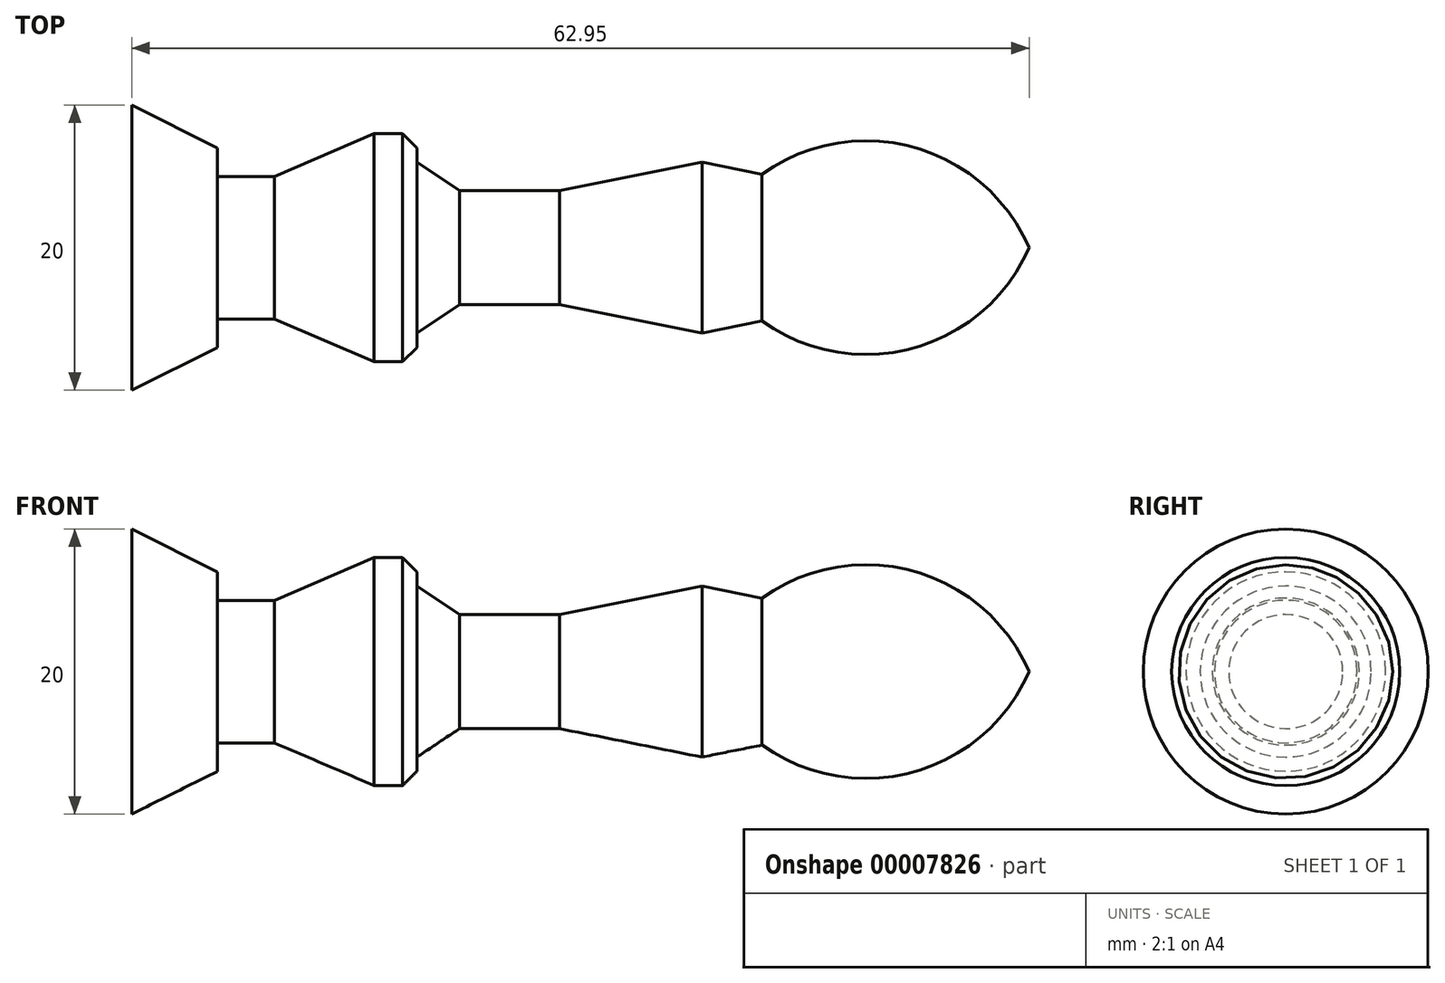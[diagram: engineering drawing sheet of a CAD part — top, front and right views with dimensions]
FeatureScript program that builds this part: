
annotation { "Feature Type Name" : "Feature", "Feature Type Description" : "" }
export const myFeature = defineFeature(function(context is Context, id is Id, definition is map)
    precondition{}
    {
        {
            var Q0;
            Q0=qCreatedBy(makeId("Front.planeOp"),FACE);
            var sketch = newSketch(context, id + "F0", { "sketchPlane" : qUnion([Q0])});
            skLineSegment(sketch, "E0", {"start": v(37.27, 0) * mm, "end": v(-27.73, 0) * mm});
            skLineSegment(sketch, "E1", {"start": v(16.48, -5.16) * mm, "end": v(12.27, -6) * mm});
            skLineSegment(sketch, "E2", {"start": v(12.27, -6) * mm, "end": v(2.27, -4) * mm});
            skLineSegment(sketch, "E3", {"start": v(2.27, -4) * mm, "end": v(-4.73, -4) * mm});
            skLineSegment(sketch, "E4", {"start": v(-4.73, -4) * mm, "end": v(-7.73, -6) * mm});
            skLineSegment(sketch, "E5", {"start": v(-7.73, -6) * mm, "end": v(-7.73, -8) * mm});
            skLineSegment(sketch, "E6", {"start": v(-7.73, -8) * mm, "end": v(-10.73, -8) * mm});
            skLineSegment(sketch, "E7", {"start": v(-10.73, -8) * mm, "end": v(-17.73, -5) * mm});
            skLineSegment(sketch, "E8", {"start": v(-17.73, -5) * mm, "end": v(-21.73, -5) * mm});
            skLineSegment(sketch, "E9", {"start": v(-21.73, -5) * mm, "end": v(-21.73, -7) * mm});
            skLineSegment(sketch, "E10", {"start": v(-21.73, -7) * mm, "end": v(-27.73, -10) * mm});
            skLineSegment(sketch, "E11", {"start": v(-27.73, -10) * mm, "end": v(-27.73, 0) * mm});
            skArc(sketch, "E12.trimOffspring", {"start": v(16.48, -5.16) * mm, "mid": v(27.08, -7.05) * mm, "end": v(35.22, 0) * mm});
            skSolve(sketch);
        }
        {
            var Q0;
            Q0=makeQuery(id+"F0.imprint","IMPRINT",FACE,{"disambiguationData":[TD([[makeQuery(id+"F0.imprint","IMPRINT",EDGE,{"derivedFrom":sQuery(id+"F0.wireOp",EDGE,"E1")}),-1.0]])]});
            var Q1;
            Q1=sQuery(id+"F0.wireOp",EDGE,"E0");
            revolve(context, id + "F1", {"entities" : qUnion([Q0]), "axis" : qUnion([Q1]), "revolveType" : RevolveType.FULL});
        }
        {
            var Q0;
            Q0=makeQuery(id+"F1.opRevolve","SWEPT_EDGE",EDGE,{"disambiguationData":[OSD([sQuery(id+"F0.wireOp",EDGE,"E5"),sQuery(id+"F0.wireOp",EDGE,"E6")])]});
            chamfer(context, id + "F2", {"entities" : qUnion([Q0]), "width" : 1 * mm});
        }
    });
